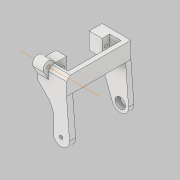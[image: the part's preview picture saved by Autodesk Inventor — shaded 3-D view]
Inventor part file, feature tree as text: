
AUTODESK INVENTOR PART (.ipt)
format: ipt  version: 2019.2 (Build 232265000, 265)  size: 273,408 bytes
history: native  units: mm
features: extrude x13, sketch x12, other x2, fillet x2, chamfer x2
ambient origin geometry x8: Origin, YZ Plane, XZ Plane, XY Plane, X Axis, Y Axis, Z Axis, Center Point
bodies: Body1 (feature_tree)
feature tree (31):
  other  "BaseTop.ipt"
  sketch  "Skizze2"  dims[d0=10.0mm d3=31.0mm]
  extrude  "Extrusion1"  Depth=10.0mm
  extrude  "Extrusion2"  Depth=25.0mm
  sketch  "Skizze16"  dims[d33=2.0mm d35=8.5mm d36=0.0mm]
  extrude  "Extrusion16"  Depth=5.5mm
  extrude  "Extrusion4"  Depth=4.0mm TaperAngle=0.0deg
  sketch  "Skizze6"  dims[d16=3.5mm d17=0.0mm d18=2.0mm]
  extrude  "LochHorn"  Depth=2.0mm
  extrude  "AussparungHorn"  Depth=7.0mm
  extrude  "BlockUnten"  Depth=4.0mm
  extrude  "BlockOben"  Depth=5.0mm TaperAngle=0.0deg
  extrude  "ServoBefestigungLöcher"  Depth=8.5mm TaperAngle=0.0deg
  extrude  "Extrusion15"  Depth=8.0mm
  extrude  "Extrusion18"  Depth=16.0mm TaperAngle=0.0deg
  fillet  "Rundung5"  Radius=16.0mm
  sketch  "Skizze22"  dims[d62=12.0mm d63=4.5mm d64=0.0mm d65=16.0mm]
  extrude  "Extrusion27"  Depth=35.0mm TaperAngle=0.0deg
  chamfer  "Fase4"  Distance=8.5mm
  extrude  "Extrusion28"  Depth=7.0mm
  other  "Arbeitsachse1"
  chamfer  "Fase5"  Distance=2.5mm
  fillet  "Rundung8"  Radius=2.5mm
  sketch  "Skizze3"  dims[d4=23.286262mm d5=25.0mm]
  sketch  "Skizze4"  dims[d6=11.0mm d9=5.5mm]
  sketch  "Skizze5"  dims[d10=4.0mm d11=0.0mm d12=4.0mm d13=0.0mm]
  sketch  "Skizze8"  dims[d19=7.0mm d20=15.0mm]
  sketch  "Skizze10"  dims[d21=4.0mm d22=2.6mm]
  sketch  "Skizze15"  dims[d25=3.25mm d26=0.0mm d31=5.0mm d32=0.0mm]
  sketch  "Skizze17"  dims[d37=8.0mm d38=0.0mm d39=2.5mm]
  sketch  "Skizze23"  dims[d66=3.0mm d67=35.0mm d68=0.0mm d69=8.5mm d70=7.0mm d71=2.5mm d72=2.5mm d73=1.5mm d74=0.0mm d75=19.5mm d76=19.0mm d77=5.0mm d78=10.0mm d79=0.0mm d81=14.0mm d112=7.0mm d115=6.0mm d116=0.0mm d124=2.1mm d125=6.0mm d126=0.0mm d130=2.5mm d131=2.0mm d132=45.0deg d133=1.0mm d134=2.0mm d135=45.0deg d136=0.25mm]
